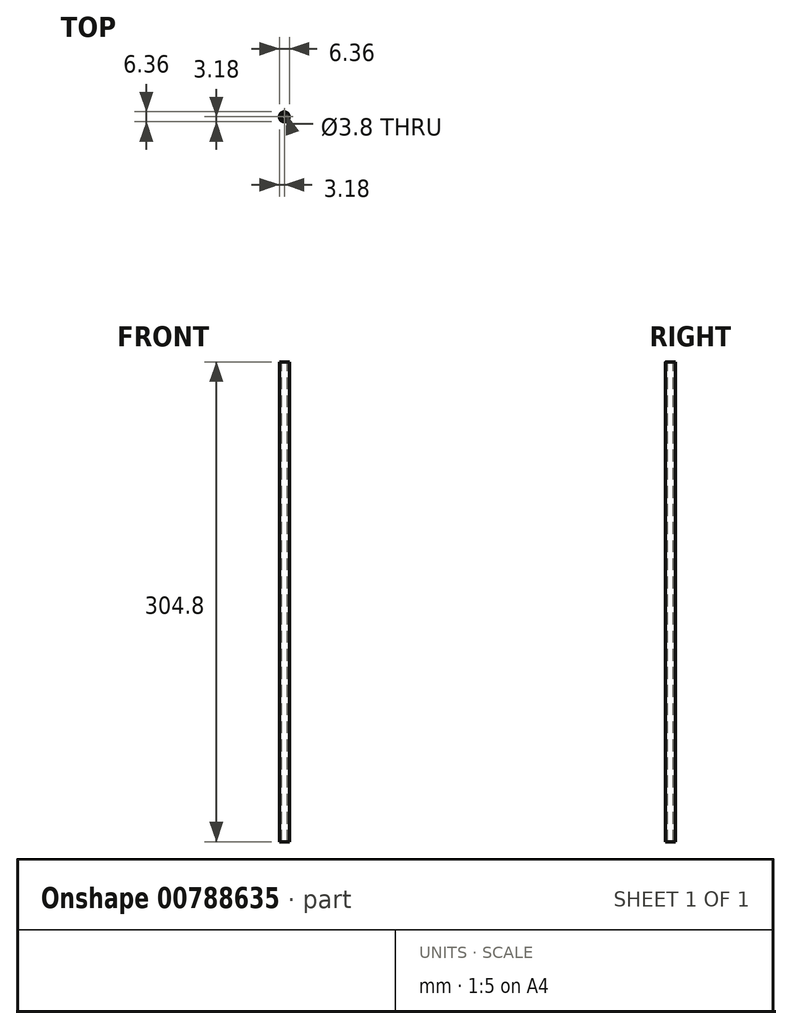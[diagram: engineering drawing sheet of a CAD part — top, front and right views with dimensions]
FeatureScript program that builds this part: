
annotation { "Feature Type Name" : "Feature", "Feature Type Description" : "" }
export const myFeature = defineFeature(function(context is Context, id is Id, definition is map)
    precondition{}
    {
        {
            var Q0;
            Q0=qCreatedBy(makeId("Top.planeOp"),FACE);
            var sketch = newSketch(context, id + "F0", { "sketchPlane" : qUnion([Q0])});
            skCircle(sketch, "E0", {"center": v(0, 0) * mm, "radius": 3.18 * mm});
            skSolve(sketch);
        }
        {
            var Q0;
            Q0=makeQuery(id+"F0.imprint","IMPRINT",FACE,{"disambiguationData":[TD([[makeQuery(id+"F0.imprint","IMPRINT",EDGE,{"derivedFrom":sQuery(id+"F0.wireOp",EDGE,"E0")}),1.0]])]});
            extrude(context, id + "F1", {"entities" : qUnion([Q0]), "depth" : 304.8 * mm, "offsetDistance" : 25.4 * mm});
        }
        {
            var Q0;
            Q0=makeQuery(id+"F1.opExtrude","CAP_FACE",FACE,{"disambiguationData":[OSD([sQuery(id+"F0.wireOp",EDGE,"E0")])],"isStart":false});
            var sketch = newSketch(context, id + "F2", { "sketchPlane" : qUnion([Q0])});
            skPoint(sketch, "E1", {"position": v(0, 0) * mm});
            skSolve(sketch);
        }
        {
            var Q0;
            Q0=sQuery(id+"F2.wireOp",VERTEX,"E1");
            var Q1;
            Q1=makeQuery(id+"F1.opExtrude","SWEPT_BODY",BODY,{"disambiguationData":[OSD([sQuery(id+"F0.wireOp",EDGE,"E0")])]});
            hole(context, id + "F3", {"style" : HoleStyle.SIMPLE, "endStyle" : HoleEndStyle.THROUGH, "standardTappedOrClearance" : lookupTablePath({ "standard" : "ANSI", "engagement" : "75%", "pitch" : "24 tpi", "size" : "#10", "type" : "Tapped" }), "standardBlindInLast" : lookupTablePath({ "standard" : "ANSI", "engagement" : "75%", "pitch" : "24 tpi", "size" : "#10", "type" : "Tapped" }), "holeDiameter" : 3.8 * mm, "majorDiameter" : 4.83 * mm, "showTappedDepth" : true, "isTappedThrough" : true, "tappedDepth" : 12.7 * mm, "tapClearance" : 3, "locations" : qUnion([Q0]), "scope" : qUnion([Q1])});
        }
    });
